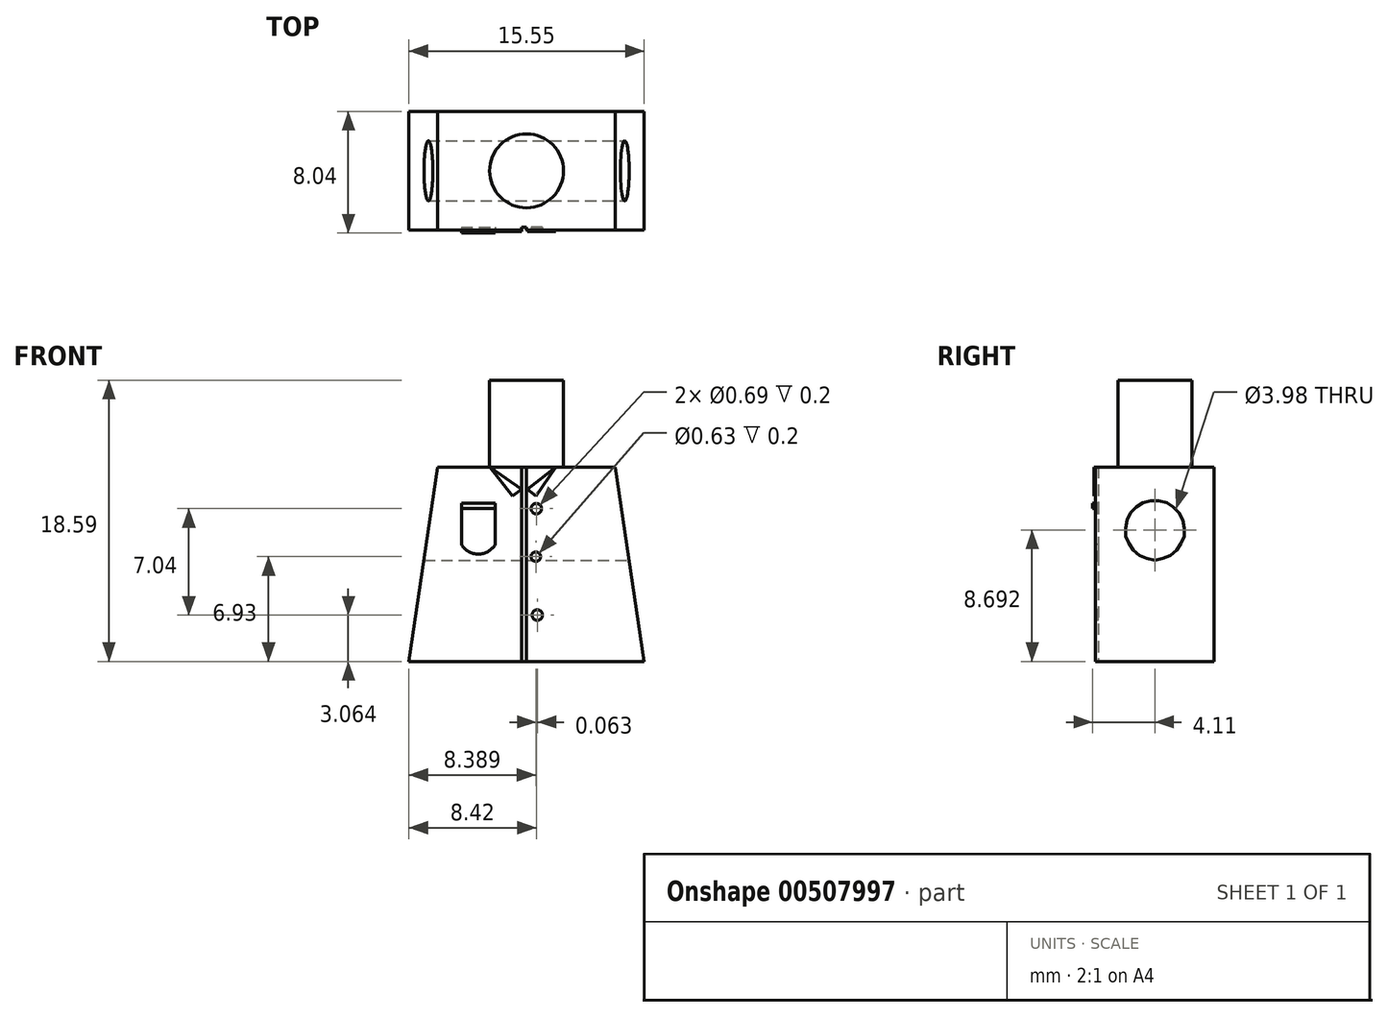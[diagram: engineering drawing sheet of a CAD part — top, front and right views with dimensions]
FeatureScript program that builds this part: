
annotation { "Feature Type Name" : "Feature", "Feature Type Description" : "" }
export const myFeature = defineFeature(function(context is Context, id is Id, definition is map)
    precondition{}
    {
        {
            var Q0;
            Q0=qCreatedBy(makeId("Front.planeOp"),FACE);
            var sketch = newSketch(context, id + "F0", { "sketchPlane" : qUnion([Q0])});
            skLineSegment(sketch, "E0.bottom", {"start": v(-49.36, 45.34) * mm, "end": v(-33.8, 45.34) * mm});
            skLineSegment(sketch, "E0.top", {"start": v(-49.36, 32.5) * mm, "end": v(-33.8, 32.5) * mm});
            skLineSegment(sketch, "E0.left", {"start": v(-49.36, 45.34) * mm, "end": v(-49.36, 32.5) * mm});
            skLineSegment(sketch, "E0.right", {"start": v(-33.8, 45.34) * mm, "end": v(-33.8, 32.5) * mm});
            skSolve(sketch);
        }
        {
            var Q0;
            Q0 = qSketchRegion(id + "F0", true);
            extrude(context, id + "F1", {"entities" : qUnion([Q0]), "depth" : 7.86 * mm, "offsetDistance" : 25 * mm});
        }
        {
            var Q0;
            Q0=makeQuery(id+"F1.opExtrude","SWEPT_FACE",FACE,{"disambiguationData":[OSD([sQuery(id+"F0.wireOp",EDGE,"E0.bottom")])]});
            var sketch = newSketch(context, id + "F2", { "sketchPlane" : qUnion([Q0])});
            skCircle(sketch, "E1", {"center": v(-41.58, -3.93) * mm, "radius": 2.44 * mm});
            skPoint(sketch, "E1.centerSnap0", {"position": v(-49.36, -3.93) * mm});
            skPoint(sketch, "E1.centerSnap1", {"position": v(-41.58, 0) * mm});
            skSolve(sketch);
        }
        {
            var Q0;
            Q0=makeQuery(id+"F2.imprint","IMPRINT",FACE,{"disambiguationData":[TD([[makeQuery(id+"F2.imprint","IMPRINT",EDGE,{"derivedFrom":sQuery(id+"F2.wireOp",EDGE,"E1")}),1.0]])]});
            extrude(context, id + "F3", {"entities" : qUnion([Q0]), "operationType" : NewBodyOperationType.ADD, "depth" : 5.74 * mm, "offsetDistance" : 25 * mm});
        }
        {
            var Q0;
            Q0=makeQuery(id+"F1.opExtrude","SWEPT_FACE",FACE,{"disambiguationData":[OSD([sQuery(id+"F0.wireOp",EDGE,"E0.right")])]});
            var sketch = newSketch(context, id + "F4", { "sketchPlane" : qUnion([Q0])});
            skCircle(sketch, "E2", {"center": v(-3.93, 41.18) * mm, "radius": 1.99 * mm});
            skPoint(sketch, "E2.centerSnap0", {"position": v(-3.93, 45.34) * mm});
            skSolve(sketch);
        }
        {
            var Q0;
            Q0 = qSketchRegion(id + "F4", true);
            extrude(context, id + "F5", {"entities" : qUnion([Q0]), "operationType" : NewBodyOperationType.REMOVE, "oppositeDirection" : true, "depth" : 25 * mm, "offsetDistance" : 25 * mm});
        }
        {
            var Q0;
            Q0=makeQuery(id+"F1.opExtrude","CAP_FACE",FACE,{"disambiguationData":[OSD([sQuery(id+"F0.wireOp",EDGE,"E0.bottom"),sQuery(id+"F0.wireOp",EDGE,"E0.top"),sQuery(id+"F0.wireOp",EDGE,"E0.left"),sQuery(id+"F0.wireOp",EDGE,"E0.right")])],"isStart":false});
            var sketch = newSketch(context, id + "F6", { "sketchPlane" : qUnion([Q0])});
            skLineSegment(sketch, "E3", {"start": v(-49.36, 32.5) * mm, "end": v(-47.46, 45.34) * mm});
            skLineSegment(sketch, "E4", {"start": v(-47.46, 45.34) * mm, "end": v(-49.36, 45.34) * mm});
            skLineSegment(sketch, "E5", {"start": v(-49.36, 45.34) * mm, "end": v(-49.36, 32.5) * mm});
            skLineSegment(sketch, "E6", {"start": v(-33.8, 32.5) * mm, "end": v(-35.7, 45.34) * mm});
            skLineSegment(sketch, "E7", {"start": v(-35.7, 45.34) * mm, "end": v(-33.8, 45.34) * mm});
            skLineSegment(sketch, "E8", {"start": v(-33.8, 45.34) * mm, "end": v(-33.8, 32.5) * mm});
            skSolve(sketch);
        }
        {
            var Q0;
            Q0=makeQuery(id+"F6.imprint","IMPRINT",FACE,{"disambiguationData":[TD([[makeQuery(id+"F6.imprint","IMPRINT",EDGE,{"derivedFrom":sQuery(id+"F6.wireOp",EDGE,"E3")}),1.0]])]});
            var Q1;
            Q1=makeQuery(id+"F6.imprint","IMPRINT",FACE,{"disambiguationData":[TD([[makeQuery(id+"F6.imprint","IMPRINT",EDGE,{"derivedFrom":sQuery(id+"F6.wireOp",EDGE,"E6")}),-1.0]])]});
            extrude(context, id + "F7", {"entities" : qUnion([Q0, Q1]), "operationType" : NewBodyOperationType.REMOVE, "oppositeDirection" : true, "depth" : 25 * mm, "offsetDistance" : 25 * mm});
        }
        {
            var Q0;
            Q0=makeQuery(id+"F1.opExtrude","CAP_FACE",FACE,{"disambiguationData":[OSD([sQuery(id+"F0.wireOp",EDGE,"E0.bottom"),sQuery(id+"F0.wireOp",EDGE,"E0.top"),sQuery(id+"F0.wireOp",EDGE,"E0.left"),sQuery(id+"F0.wireOp",EDGE,"E0.right")])],"isStart":false});
            var sketch = newSketch(context, id + "F8", { "sketchPlane" : qUnion([Q0])});
            skCircle(sketch, "E9", {"center": v(-40.94, 42.6) * mm, "radius": 0.35 * mm});
            skCircle(sketch, "E10", {"center": v(-40.97, 39.42) * mm, "radius": 0.31 * mm});
            skCircle(sketch, "E11", {"center": v(-40.88, 35.55) * mm, "radius": 0.35 * mm});
            skLineSegment(sketch, "E12.bottom", {"start": v(-41.58, 45.34) * mm, "end": v(-41.92, 45.34) * mm});
            skLineSegment(sketch, "E12.top", {"start": v(-41.58, 32.5) * mm, "end": v(-41.92, 32.5) * mm});
            skLineSegment(sketch, "E12.left", {"start": v(-41.58, 45.34) * mm, "end": v(-41.58, 32.5) * mm});
            skLineSegment(sketch, "E12.right", {"start": v(-41.92, 45.34) * mm, "end": v(-41.92, 32.5) * mm});
            skSolve(sketch);
        }
        {
            var Q0;
            Q0=makeQuery(id+"F8.imprint","IMPRINT",FACE,{"disambiguationData":[TD([[makeQuery(id+"F8.imprint","IMPRINT",EDGE,{"derivedFrom":sQuery(id+"F8.wireOp",EDGE,"E10")}),1.0]])]});
            var Q1;
            Q1=makeQuery(id+"F8.imprint","IMPRINT",FACE,{"disambiguationData":[TD([[makeQuery(id+"F8.imprint","IMPRINT",EDGE,{"derivedFrom":sQuery(id+"F8.wireOp",EDGE,"E9")}),1.0]])]});
            var Q2;
            Q2=makeQuery(id+"F8.imprint","IMPRINT",FACE,{"disambiguationData":[TD([[makeQuery(id+"F8.imprint","IMPRINT",EDGE,{"derivedFrom":sQuery(id+"F8.wireOp",EDGE,"E11")}),1.0]])]});
            extrude(context, id + "F9", {"entities" : qUnion([Q0, Q1, Q2]), "operationType" : NewBodyOperationType.REMOVE, "oppositeDirection" : true, "depth" : 0.2 * mm, "offsetDistance" : 25 * mm});
        }
        {
            var Q0;
            Q0 = qSketchRegion(id + "F8", true);
            extrude(context, id + "F10", {"entities" : qUnion([Q0]), "operationType" : NewBodyOperationType.REMOVE, "oppositeDirection" : true, "depth" : 0.2 * mm, "offsetDistance" : 25 * mm});
        }
        {
            var Q0;
            {var subQ0=sQuery(id+"F0.wireOp",EDGE,"E0.bottom");var subQ1=sQuery(id+"F0.wireOp",EDGE,"E0.top");Q0=makeQuery(id+"F10.boolean.opBoolean","SPLIT",FACE,{"disambiguationData":[TD([makeQuery(id+"F7.boolean.opBoolean","COPY",FACE,{"derivedFrom":makeQuery(id+"F7.opExtrude","SWEPT_FACE",FACE,{"disambiguationData":[OSD([sQuery(id+"F6.wireOp",EDGE,"E3")])]})})])],"derivedFrom":makeQuery(id+"F1.opExtrude","CAP_FACE",FACE,{"disambiguationData":[OSD([subQ0,subQ1,sQuery(id+"F0.wireOp",EDGE,"E0.left"),sQuery(id+"F0.wireOp",EDGE,"E0.right")])],"isStart":false})});}
            var sketch = newSketch(context, id + "F11", { "sketchPlane" : qUnion([Q0])});
            skLineSegment(sketch, "E13", {"start": v(-41.92, 43.89) * mm, "end": v(-42.52, 43.42) * mm});
            skLineSegment(sketch, "E14", {"start": v(-42.52, 43.42) * mm, "end": v(-44.01, 45.34) * mm});
            skLineSegment(sketch, "E15", {"start": v(-44.01, 45.34) * mm, "end": v(-41.92, 43.89) * mm});
            skLineSegment(sketch, "E16", {"start": v(-41.53, 43.89) * mm, "end": v(-39.66, 45.34) * mm});
            skLineSegment(sketch, "E17", {"start": v(-39.66, 45.34) * mm, "end": v(-40.95, 43.42) * mm});
            skLineSegment(sketch, "E18", {"start": v(-40.95, 43.42) * mm, "end": v(-41.53, 43.89) * mm});
            skSolve(sketch);
        }
        {
            var Q0;
            Q0=makeQuery(id+"F11.imprint","IMPRINT",FACE,{"disambiguationData":[TD([[makeQuery(id+"F11.imprint","IMPRINT",EDGE,{"derivedFrom":sQuery(id+"F11.wireOp",EDGE,"E13")}),-1.0]])]});
            var Q1;
            Q1=makeQuery(id+"F11.imprint","IMPRINT",FACE,{"disambiguationData":[TD([[makeQuery(id+"F11.imprint","IMPRINT",EDGE,{"derivedFrom":sQuery(id+"F11.wireOp",EDGE,"E16")}),-1.0]])]});
            extrude(context, id + "F12", {"entities" : qUnion([Q0, Q1]), "operationType" : NewBodyOperationType.ADD, "depth" : 0.1 * mm, "offsetDistance" : 25 * mm});
        }
        {
            var Q0;
            {var subQ0=sQuery(id+"F0.wireOp",EDGE,"E0.top");var subQ1=makeQuery(id+"F1.opExtrude","SWEPT_FACE",FACE,{"disambiguationData":[OSD([subQ0])]});var subQ2=makeQuery(id+"F7.boolean.opBoolean","COPY",FACE,{"derivedFrom":makeQuery(id+"F7.opExtrude","SWEPT_FACE",FACE,{"disambiguationData":[OSD([sQuery(id+"F6.wireOp",EDGE,"E3")])]})});var subQ3=sQuery(id+"F0.wireOp",EDGE,"E0.bottom");var subQ4=makeQuery(id+"F1.opExtrude","CAP_FACE",FACE,{"disambiguationData":[OSD([subQ3,subQ0,sQuery(id+"F0.wireOp",EDGE,"E0.left"),sQuery(id+"F0.wireOp",EDGE,"E0.right")])],"isStart":false});var subQ5=makeQuery(id+"F1.opExtrude","SWEPT_FACE",FACE,{"disambiguationData":[OSD([subQ3])]});var subQ6=makeQuery(id+"F10.opExtrude","SWEPT_FACE",FACE,{"disambiguationData":[OSD([sQuery(id+"F8.wireOp",EDGE,"E12.right")])]});Q0=makeQuery(id+"F12.boolean.opBoolean","SPLIT",FACE,{"disambiguationData":[TD([subQ5,subQ4,subQ1,subQ2,makeQuery(id+"F10.boolean.opBoolean","COPY",FACE,{"derivedFrom":subQ6}),makeQuery(id+"F12.opExtrude","SWEPT_FACE",FACE,{"disambiguationData":[OSD([sQuery(id+"F11.wireOp",EDGE,"E13")])]}),makeQuery(id+"F12.opExtrude","SWEPT_FACE",FACE,{"disambiguationData":[OSD([sQuery(id+"F11.wireOp",EDGE,"E14")])]}),makeQuery(id+"F12.opExtrude","SWEPT_FACE",FACE,{"disambiguationData":[OSD([sQuery(id+"F11.wireOp",EDGE,"E15")])]})])],"derivedFrom":makeQuery(id+"F10.boolean.opBoolean","SPLIT",FACE,{"disambiguationData":[TD([subQ2])],"derivedFrom":subQ4})});}
            var sketch = newSketch(context, id + "F13", { "sketchPlane" : qUnion([Q0])});
            skLineSegment(sketch, "E19.bottom", {"start": v(-45.89, 42.96) * mm, "end": v(-43.66, 42.96) * mm});
            skLineSegment(sketch, "E19.left", {"start": v(-45.89, 42.96) * mm, "end": v(-45.89, 40.22) * mm});
            skLineSegment(sketch, "E19.right", {"start": v(-43.66, 42.96) * mm, "end": v(-43.66, 40.22) * mm});
            skLineSegment(sketch, "E20.bottom", {"start": v(-45.89, 42.6) * mm, "end": v(-43.66, 42.6) * mm});
            skLineSegment(sketch, "E20.left", {"start": v(-45.89, 42.6) * mm, "end": v(-45.89, 42.96) * mm});
            skLineSegment(sketch, "E20.right", {"start": v(-43.66, 42.6) * mm, "end": v(-43.66, 42.96) * mm});
            skArc(sketch, "E21", {"start": v(-45.89, 40.22) * mm, "mid": v(-44.77, 39.6) * mm, "end": v(-43.66, 40.22) * mm});
            skSolve(sketch);
        }
        {
            var Q0;
            Q0=makeQuery(id+"F13.imprint","IMPRINT",FACE,{"disambiguationData":[TD([[makeQuery(id+"F13.imprint","IMPRINT",EDGE,{"derivedFrom":sQuery(id+"F13.wireOp",EDGE,"E20.bottom")}),1.0]])]});
            extrude(context, id + "F14", {"entities" : qUnion([Q0]), "operationType" : NewBodyOperationType.ADD, "depth" : 0.18 * mm, "offsetDistance" : 25 * mm});
        }
        {
            var Q0;
            Q0=makeQuery(id+"F13.imprint","IMPRINT",FACE,{"disambiguationData":[TD([[makeQuery(id+"F13.imprint","IMPRINT",EDGE,{"derivedFrom":sQuery(id+"F13.wireOp",EDGE,"E19.left")}),1.0]])]});
            extrude(context, id + "F15", {"entities" : qUnion([Q0]), "operationType" : NewBodyOperationType.REMOVE, "oppositeDirection" : true, "depth" : 0.2 * mm, "offsetDistance" : 25 * mm});
        }
    });
